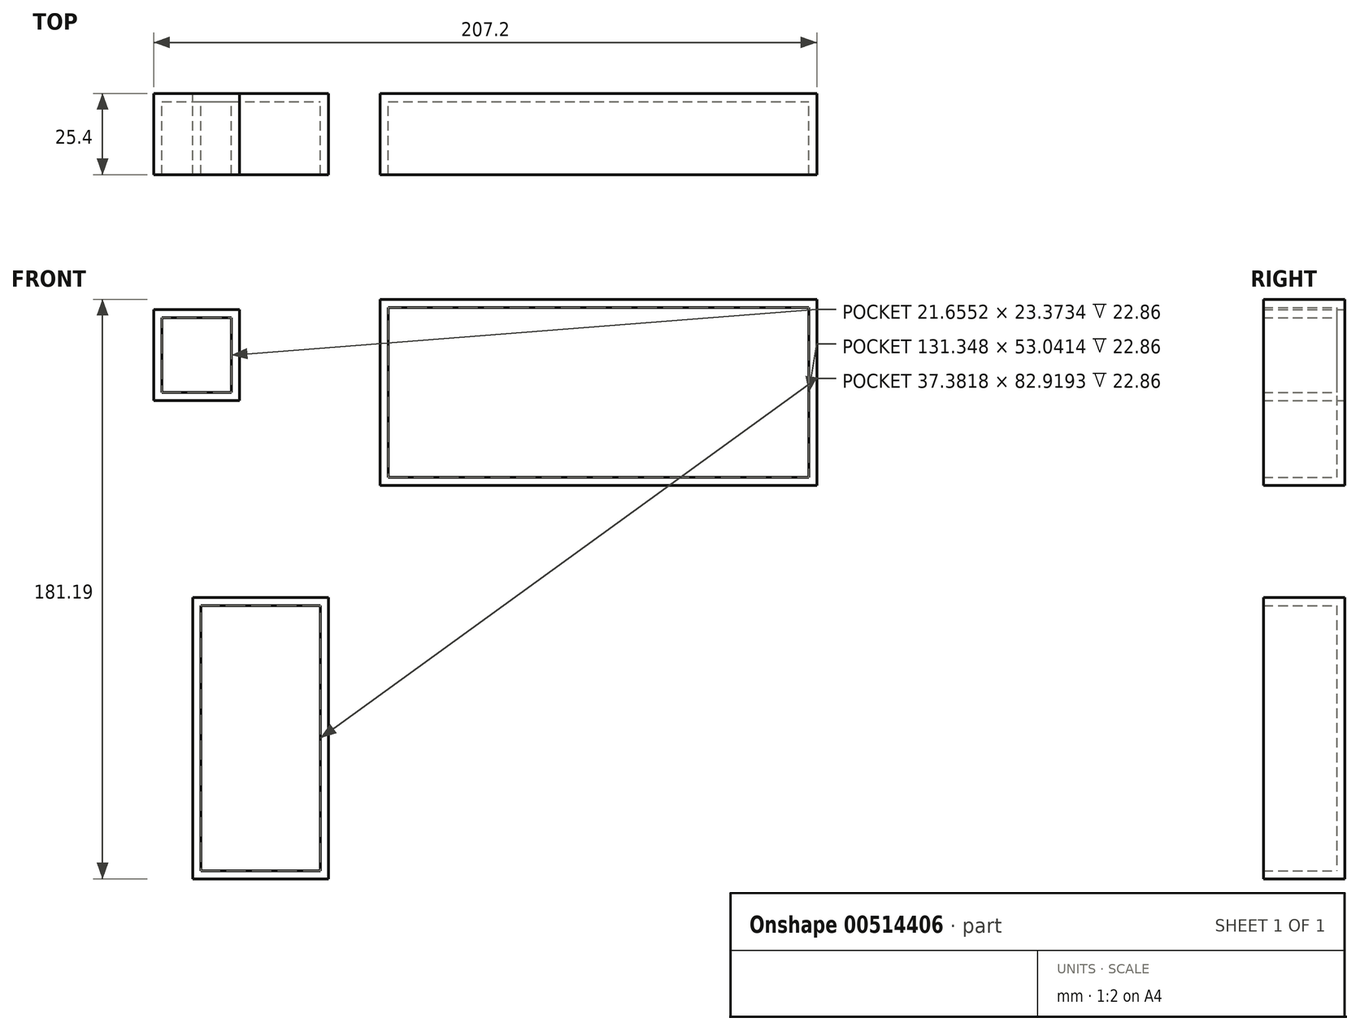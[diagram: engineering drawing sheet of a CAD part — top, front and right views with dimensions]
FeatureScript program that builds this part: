
annotation { "Feature Type Name" : "Feature", "Feature Type Description" : "" }
export const myFeature = defineFeature(function(context is Context, id is Id, definition is map)
    precondition{}
    {
        {
            var Q0;
            Q0=qCreatedBy(makeId("Front.planeOp"),FACE);
            var sketch = newSketch(context, id + "F0", { "sketchPlane" : qUnion([Q0])});
            skLineSegment(sketch, "E0.bottom", {"start": v(-86.3, 65.9) * mm, "end": v(-59.56, 65.9) * mm});
            skLineSegment(sketch, "E0.top", {"start": v(-86.3, 37.46) * mm, "end": v(-59.56, 37.46) * mm});
            skLineSegment(sketch, "E0.left", {"start": v(-86.3, 65.9) * mm, "end": v(-86.3, 37.46) * mm});
            skLineSegment(sketch, "E0.right", {"start": v(-59.56, 65.9) * mm, "end": v(-59.56, 37.46) * mm});
            skLineSegment(sketch, "E1.bottom", {"start": v(-15.53, 69.04) * mm, "end": v(120.9, 69.04) * mm});
            skLineSegment(sketch, "E1.top", {"start": v(-15.53, 10.92) * mm, "end": v(120.9, 10.92) * mm});
            skLineSegment(sketch, "E1.left", {"start": v(-15.53, 69.04) * mm, "end": v(-15.53, 10.92) * mm});
            skLineSegment(sketch, "E1.right", {"start": v(120.9, 69.04) * mm, "end": v(120.9, 10.92) * mm});
            skLineSegment(sketch, "E2.bottom", {"start": v(-74.11, -24.15) * mm, "end": v(-31.65, -24.15) * mm});
            skLineSegment(sketch, "E2.top", {"start": v(-74.11, -112.15) * mm, "end": v(-31.65, -112.15) * mm});
            skLineSegment(sketch, "E2.left", {"start": v(-74.11, -24.15) * mm, "end": v(-74.11, -112.15) * mm});
            skLineSegment(sketch, "E2.right", {"start": v(-31.65, -24.15) * mm, "end": v(-31.65, -112.15) * mm});
            skSolve(sketch);
        }
        {
            var Q0;
            Q0 = qSketchRegion(id + "F0", true);
            extrude(context, id + "F1", {"entities" : qUnion([Q0]), "depth" : 25.4 * mm});
        }
        {
            var Q0;
            Q0=makeQuery(id+"F1.opExtrude","CAP_FACE",FACE,{"disambiguationData":[OSD([sQuery(id+"F0.wireOp",EDGE,"E0.bottom"),sQuery(id+"F0.wireOp",EDGE,"E0.top"),sQuery(id+"F0.wireOp",EDGE,"E0.left"),sQuery(id+"F0.wireOp",EDGE,"E0.right")])],"isStart":false});
            var Q1;
            Q1=makeQuery(id+"F1.opExtrude","CAP_FACE",FACE,{"disambiguationData":[OSD([sQuery(id+"F0.wireOp",EDGE,"E1.bottom"),sQuery(id+"F0.wireOp",EDGE,"E1.top"),sQuery(id+"F0.wireOp",EDGE,"E1.left"),sQuery(id+"F0.wireOp",EDGE,"E1.right")])],"isStart":false});
            var Q2;
            Q2=makeQuery(id+"F1.opExtrude","CAP_FACE",FACE,{"disambiguationData":[OSD([sQuery(id+"F0.wireOp",EDGE,"E2.bottom"),sQuery(id+"F0.wireOp",EDGE,"E2.top"),sQuery(id+"F0.wireOp",EDGE,"E2.left"),sQuery(id+"F0.wireOp",EDGE,"E2.right")])],"isStart":false});
            shell(context, id + "F2", {"entities" : qUnion([Q0, Q1, Q2]), "thickness" : 2.54 * mm});
        }
    });
